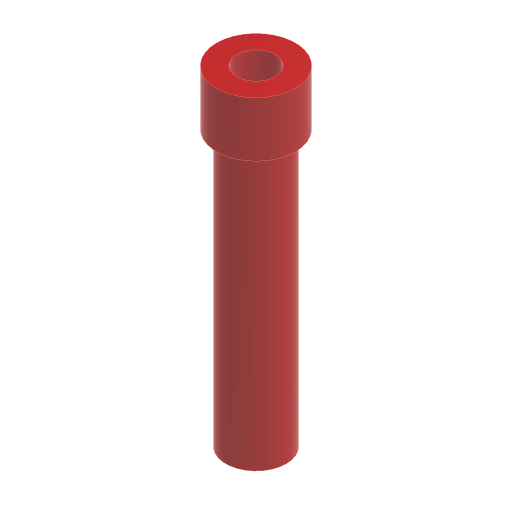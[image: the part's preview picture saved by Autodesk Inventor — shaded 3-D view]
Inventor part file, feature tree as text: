
AUTODESK INVENTOR PART (.ipt)
format: ipt  version: 2024.3 (Build 283343000, 343)  size: 257,536 bytes
history: native  units: mm
features: extrude x2, sketch x2, projected_geometry x1
ambient origin geometry x8: Origin, YZ Plane, XZ Plane, XY Plane, X Axis, Y Axis, Z Axis, Center Point
bodies: Solid1 (feature_tree)
feature tree (5):
  extrude  "Extrusion1"  Depth=2.1mm
  extrude  "Extrusion2"  Depth=3.0mm
  sketch  "Sketch1"  dims[d0=3.3mm d1=2.1mm]
  sketch  "Sketch2"  dims[d2=15.0mm d3=0.0mm d4=0.5mm d5=3.0mm d6=0.0mm]
  projected_geometry  "Projected Loop1"
